# Revit family: AUU-AQT-363-50-50-C-S-left-NCM
name_source: partatom
category: Оборудование
revit_build: Autodesk Revit 2018 (Build: 20170223_1515(x64)
units: mm (PartAtom-declared; Revit-internal decimal feet)

## family parameters
Всегда вертикально = Да
Классификация = Нет
На основе рабочей плоскости = Нет
Общий = Нет
При загрузке вырезать с полостями = Нет
Размер круглого соединителя = Использовать диаметр
Тип детали = Нормальный
Точка расчета площади = Нет

## types (1)
- АУУ-AQT-363-50-50-C-S Лев NCM
    ADSK_Версия Revit = 2018
    ADSK_Версия семейства = v2
    ADSK_Единица измерения = шт.
    ADSK_Завод-изготовитель = Danfoss
    ADSK_Код изделия = 150U3531
    ADSK_Количество = 1
    ADSK_Марка = АУУ-AQT-363-50-50-C-S Лев NCM
    ADSK_Масса = 0
    ADSK_Наименование = Узел смесительный АУУ-AQT-363-50-50-C-S Лев NCM для регулирования воздухонагревателей первого подогрева, PN10, Tmax=120, с подключением от источника с левой стороны, в составе: комбинированный клапан AQT DN50, электропривод NovoCon M, насос Magna1 40-80F, запорная арматура DN50, сетчатый фильтр с дренажом DN50, балансировочный клапан внутр. контура MVT DN50, перемычка с обратным клапаном, устройство для выпуска воздуха, термоманометры, кронштейн для крепления к стене
    ADSK_Наименование краткое = АУУ-AQT-363-50-50-C-S Лев NCM
    ADSK_Обозначение = АУУ-AQT-363-50-50-C-S Лев NCM
    ADSK_Размер_Диаметр = 50 мм
    D_pipe = 59 мм
    H = 337 мм
    Kvs балансировочного клапана = 40
    L = 1500 мм
    Tmax = 120 °C
    URL = https://www.danfoss.com
    Диаметр балансировочного клапана = DN50
    Диаметр ввода = 50 мм
    Диаметр присоединения к калориферу = 50 мм
    Диаметр регулирующего клапана = DN50
    Допустимые среды = Вода, подготовленная для систем теплоснабжения
    Изготовитель = Danfoss
    Изготовитель (телефон) = +7(495)792-57-57
    Номинальный расход комбинированого клапана = 12.5 м³/ч
    Особенность привода = NovoCon
    Привод = NovoCon M
    Разработчик = ООО ПРОРУБИМ
    Разработчик (URL) = http://prorubim.com
    Разработчик (телефон) = +7(495)649-85-43
    Сторона подключения (от источника) = Левая
    Тип балансировочного клапана = MVT
    Тип насоса = Magna1 40-80F
    Тип регулирующего клапана = AQT
    Условное давление = 10000.0 кПа

## geometry (parser evidence)
native form markers: Sweep x11
no freeform markers — native parametric forms only
